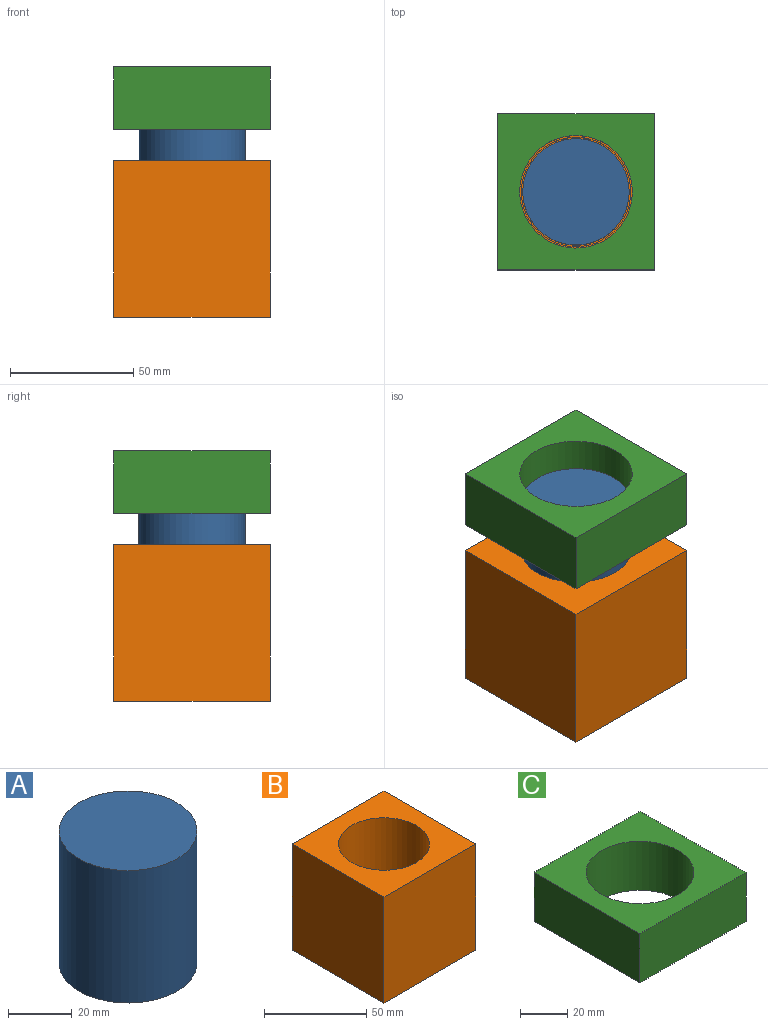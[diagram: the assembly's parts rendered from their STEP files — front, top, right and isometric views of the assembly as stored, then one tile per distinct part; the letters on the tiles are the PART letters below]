
ASSEMBLY  parts=3 mates=2
PART A: 3 faces, bbox 43.2x43.2x50.8 mm
  f0: cylinder r=21.59mm len=50.8mm, axis (0,0,-1), area 6891.2mm2, adj f1,f2
  f1: plane 43.18x43.18mm, normal (0,0,1), area 1464.4mm2, adj f0
  f2: plane 43.18x43.18mm, normal (0,0,-1), area 1464.4mm2, adj f0
PART B: 8 faces, bbox 63.5x63.5x63.5 mm
  f0: plane 63.5x63.5mm, normal (0,-1,0), area 4032.3mm2, adj f1,f3,f4,f5
  f1: plane 63.5x63.5mm, normal (1,0,0), area 4032.3mm2, adj f0,f2,f4,f5
  f2: plane 63.5x63.5mm, normal (0,1,0), area 4032.3mm2, adj f1,f3,f4,f5
  f3: plane 63.5x63.5mm, normal (-1,0,0), area 4032.3mm2, adj f0,f2,f4,f5
  f4: plane 63.5x63.5mm, normal (0,0,1), area 2480.5mm2, adj f0,f1,f2,f3,f6
  f5: plane 63.5x63.5mm, normal (0,0,-1), area 4032.3mm2, adj f0,f1,f2,f3
  f6: cylinder r=22.23mm len=50.8mm, axis (0,0,1), area 7093.9mm2, adj f4,f7
  f7: plane 44.45x44.45mm, normal (0,0,1), area 1551.8mm2, adj f6
PART C: 7 faces, bbox 63.5x63.5x25.4 mm
  f0: plane 63.5x25.4mm, normal (-1,0,0), area 1612.9mm2, adj f1,f3,f5,f6
  f1: plane 63.5x25.4mm, normal (0,-1,0), area 1612.9mm2, adj f0,f2,f5,f6
  f2: plane 63.5x25.4mm, normal (1,0,0), area 1612.9mm2, adj f1,f3,f5,f6
  f3: plane 63.5x25.4mm, normal (0,1,0), area 1612.9mm2, adj f0,f2,f5,f6
  f4: cylinder r=22.86mm len=45.72mm, axis (0,0,-1), area 3648.3mm2, adj f5,f6
  f5: plane 63.5x63.5mm, normal (0,0,1), area 2390.5mm2, adj f0,f1,f2,f3,f4
  f6: plane 63.5x63.5mm, normal (0,0,-1), area 2390.5mm2, adj f0,f1,f2,f3,f4
PLACE A t=(0.22,-2.06,-2.8)mm
PLACE B t=(0.22,-2.06,-2.8)mm
PLACE C t=(0.22,-2.06,7.36)mm
MATE revolute A.f0 <-> B.f6  axis (0,0,-1) through (0.22,-2.06,60.7)mm
MATE revolute C.f4 <-> A.f0  axis (0,0,-1) through (0.22,-2.06,86.1)mm
